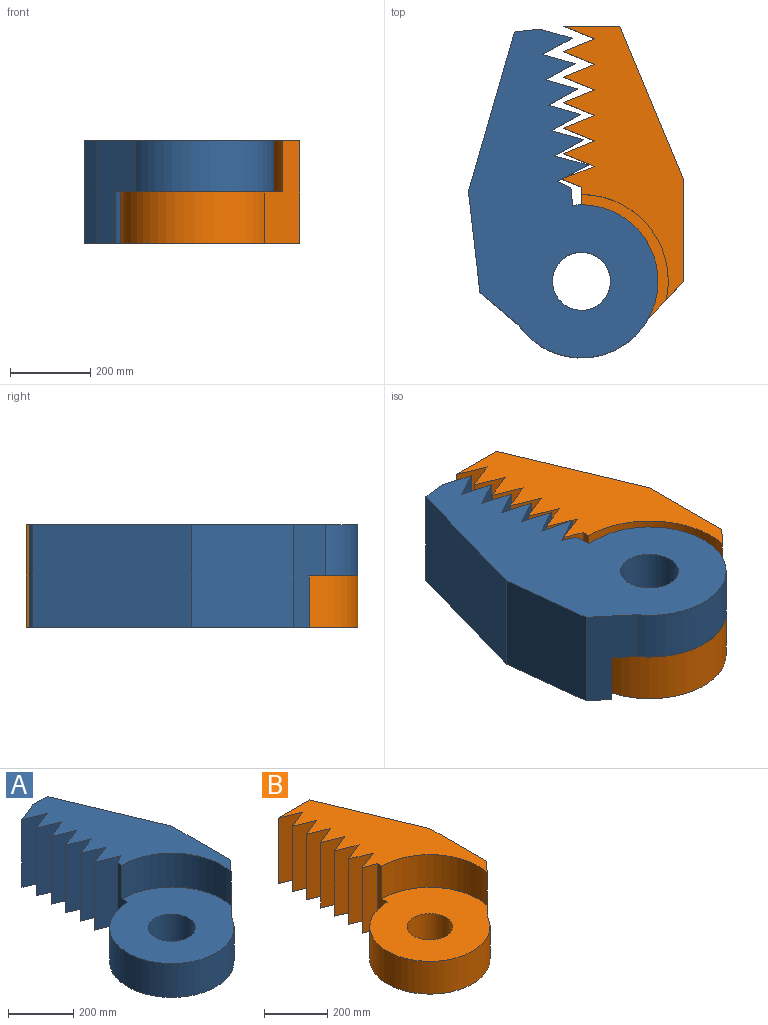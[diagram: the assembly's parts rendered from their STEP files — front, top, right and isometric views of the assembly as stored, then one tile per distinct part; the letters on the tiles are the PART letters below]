
ASSEMBLY  parts=2 mates=1
PART A: 24 faces, bbox 444.5x825.5x254 mm
  f0: plane 406.4x406.4mm, normal (0,0,1), area 107469.2mm2, adj f1,f6,f7,f9,f23
  f1: plane 254x92.23mm, normal (0.73,-0.69,0), area 24055.9mm2, adj f0,f2,f7,f8,f9,f10
  f2: plane 254x254mm, normal (1,0,0), area 64516mm2, adj f1,f3,f8,f10
  f3: plane 381x254mm, normal (0.92,0.38,0), area 104838.5mm2, adj f2,f4,f8,f10
  f4: plane 254x63.5mm, normal (0,1,0), area 16129mm2, adj f3,f8,f10,f13
  f5: plane 254x31.75mm, normal (-0.54,0.84,0), area 9561.1mm2, adj f6,f8,f10,f22
  f6: plane 254x43.28mm, normal (-1,0,0), area 7767.1mm2, adj f0,f5,f7,f8,f9,f10
  f7: cylinder r=190.5mm len=381mm, axis (0,0,-1), area 101782.7mm2, adj f0,f1,f6,f8
  f8: plane 825.5x444.5mm, normal (0,0,-1), area 205206.1mm2, adj f1,f2,f3,f4,f5,f6,f7,f11
  f9: cylinder r=215.9mm len=261.23mm, axis (0,0,-1), area 48869.7mm2, adj f0,f1,f6,f10
  f10: plane 680.33x303.62mm, normal (0,0,1), area 97736.9mm2, adj f1,f2,f3,f4,f5,f6,f9,f11
  f11: plane 254x77.52mm, normal (-0.38,0.93,0), area 21277.2mm2, adj f8,f10,f12,f14
  f12: plane 254x77.52mm, normal (-0.38,-0.93,0), area 21277.2mm2, adj f8,f10,f11,f15
  f13: plane 254x77.52mm, normal (-0.38,0.93,0), area 21277.2mm2, adj f4,f8,f10,f14
  f14: plane 254x77.52mm, normal (-0.38,-0.93,0), area 21277.2mm2, adj f8,f10,f11,f13
  f15: plane 254x77.52mm, normal (-0.38,0.93,0), area 21277.2mm2, adj f8,f10,f12,f16
  f16: plane 254x77.52mm, normal (-0.38,-0.93,0), area 21277.2mm2, adj f8,f10,f15,f17
  f17: plane 254x77.52mm, normal (-0.38,0.93,0), area 21277.2mm2, adj f8,f10,f16,f18
  f18: plane 254x77.52mm, normal (-0.38,-0.93,0), area 21277.2mm2, adj f8,f10,f17,f19
  f19: plane 254x77.52mm, normal (-0.38,0.93,0), area 21277.2mm2, adj f8,f10,f18,f20
  f20: plane 254x77.52mm, normal (-0.38,-0.93,0), area 21277.2mm2, adj f8,f10,f19,f21
  f21: plane 254x81.37mm, normal (-0.36,0.93,0), area 22184.5mm2, adj f8,f10,f20,f22
  f22: plane 254x81.37mm, normal (-0.36,-0.93,0), area 22184.5mm2, adj f5,f8,f10,f21
  f23: cylinder r=72.17mm len=144.34mm, axis (0,0,1), area 57589.6mm2, adj f0,f8
PART B: 25 faces, bbox 444.5x825.5x254 mm
  f0: plane 254x0.84mm, normal (-0.54,0.84,0), area 252.2mm2, adj f6,f8,f10,f20
  f1: plane 406.4x406.4mm, normal (0,0,1), area 107469.2mm2, adj f2,f6,f7,f9,f24
  f2: plane 254x92.23mm, normal (0.73,-0.69,0), area 24055.9mm2, adj f1,f3,f7,f8,f9,f10
  f3: plane 254x254mm, normal (1,0,0), area 64516mm2, adj f2,f4,f8,f10
  f4: plane 381x254mm, normal (0.92,0.38,0), area 104838.5mm2, adj f3,f5,f8,f10
  f5: plane 254x141.02mm, normal (0,1,0), area 35818.6mm2, adj f4,f8,f10,f13
  f6: plane 254x43.28mm, normal (-1,0,0), area 7767.1mm2, adj f0,f1,f7,f8,f9,f10
  f7: cylinder r=190.5mm len=381mm, axis (0,0,-1), area 101782.7mm2, adj f1,f2,f6,f8
  f8: plane 825.5x444.5mm, normal (0,0,-1), area 205946mm2, adj f0,f2,f3,f4,f5,f6,f7,f11
  f9: cylinder r=215.9mm len=261.23mm, axis (0,0,-1), area 48869.7mm2, adj f1,f2,f6,f10
  f10: plane 680.33x303.62mm, normal (0,0,1), area 98476.8mm2, adj f0,f2,f3,f4,f5,f6,f9,f11
  f11: plane 254x77.52mm, normal (-0.38,0.93,0), area 21277.2mm2, adj f8,f10,f12,f23
  f12: plane 254x77.52mm, normal (-0.38,-0.93,0), area 21277.2mm2, adj f8,f10,f11,f14
  f13: plane 254x77.52mm, normal (-0.38,-0.93,0), area 21277.2mm2, adj f5,f8,f10,f22
  f14: plane 254x77.52mm, normal (-0.38,0.93,0), area 21277.2mm2, adj f8,f10,f12,f15
  f15: plane 254x77.52mm, normal (-0.38,-0.93,0), area 21277.2mm2, adj f8,f10,f14,f16
  f16: plane 254x77.52mm, normal (-0.38,0.93,0), area 21277.2mm2, adj f8,f10,f15,f17
  f17: plane 254x77.52mm, normal (-0.38,-0.93,0), area 21277.2mm2, adj f8,f10,f16,f18
  f18: plane 254x77.52mm, normal (-0.38,0.93,0), area 21277.2mm2, adj f8,f10,f17,f19
  f19: plane 254x77.52mm, normal (-0.38,-0.93,0), area 21277.2mm2, adj f8,f10,f18,f21
  f20: plane 254x50.45mm, normal (-0.36,-0.93,0), area 13756.1mm2, adj f0,f8,f10,f21
  f21: plane 254x81.37mm, normal (-0.36,0.93,0), area 22184.5mm2, adj f8,f10,f19,f20
  f22: plane 254x77.52mm, normal (-0.38,0.93,0), area 21277.2mm2, adj f8,f10,f13,f23
  f23: plane 254x77.52mm, normal (-0.38,-0.93,0), area 21277.2mm2, adj f8,f10,f11,f22
  f24: cylinder r=72.17mm len=144.34mm, axis (0,0,1), area 57589.6mm2, adj f1,f8
PLACE A rot(axis=(-0.06,1,0),180deg) t=(-215.6,-207.22,308.83)mm
PLACE B t=(-215.6,-207.22,54.83)mm fixed
MATE revolute A.f7 <-> B.f7  axis (0,0,-1) through (-215.6,-207.22,181.83)mm
